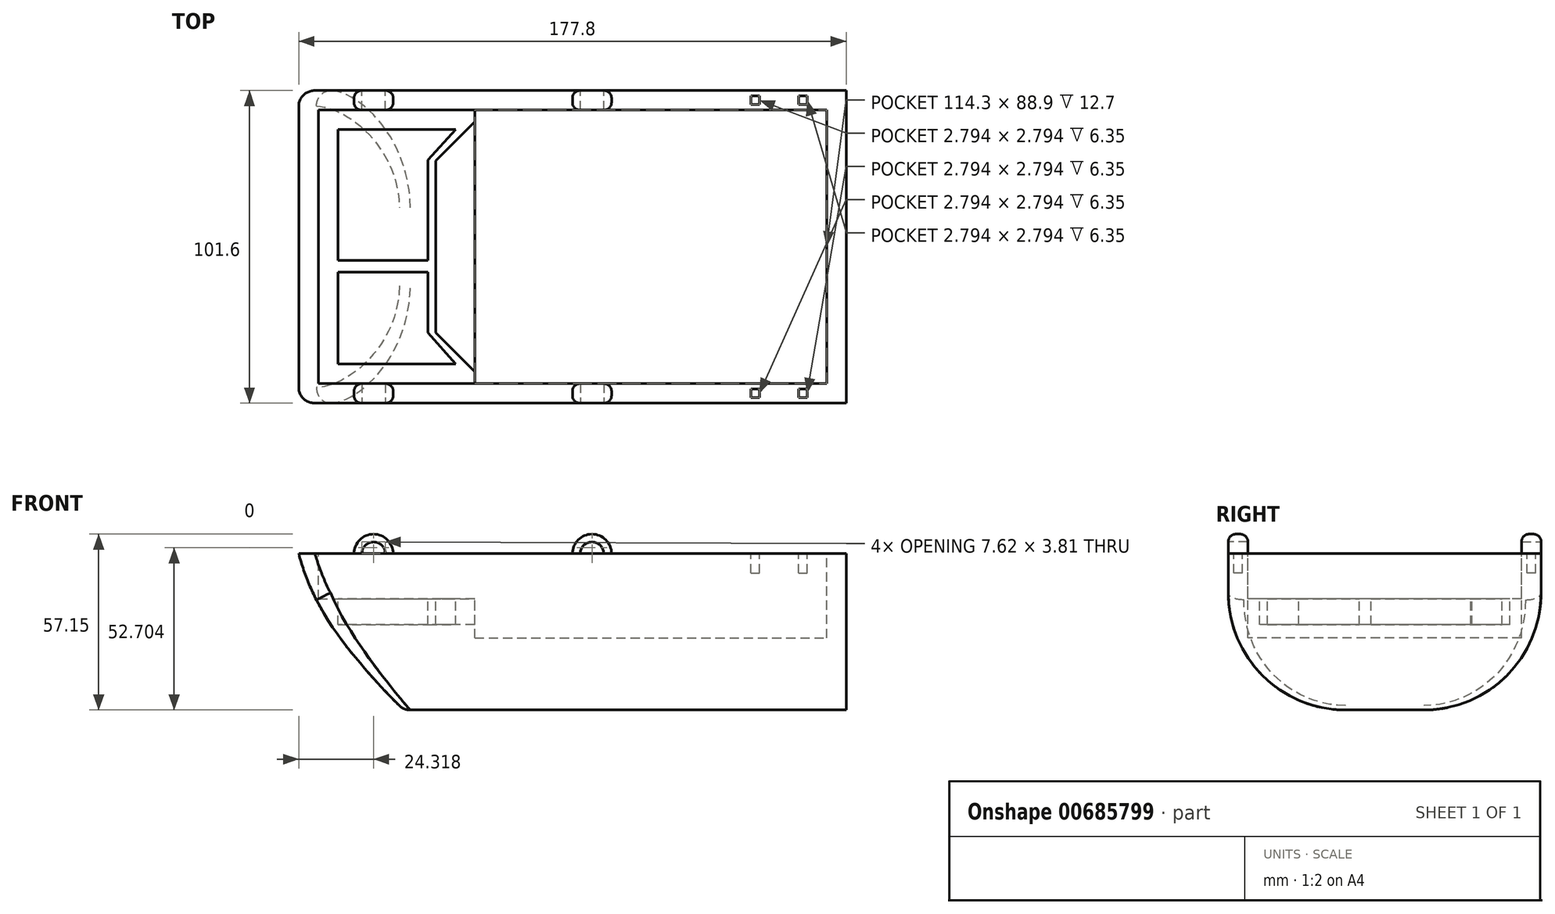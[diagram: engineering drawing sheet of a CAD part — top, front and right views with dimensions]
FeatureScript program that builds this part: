
annotation { "Feature Type Name" : "Feature", "Feature Type Description" : "" }
export const myFeature = defineFeature(function(context is Context, id is Id, definition is map)
    precondition{}
    {
        {
            var Q0;
            Q0=qCreatedBy(makeId("Front.planeOp"),FACE);
            var sketch = newSketch(context, id + "F0", { "sketchPlane" : qUnion([Q0])});
            skLineSegment(sketch, "E0.bottom", {"start": v(-88.38, 8.83) * mm, "end": v(89.42, 8.83) * mm});
            skLineSegment(sketch, "E0.top", {"start": v(-88.38, -41.97) * mm, "end": v(89.42, -41.97) * mm});
            skLineSegment(sketch, "E0.left", {"start": v(-88.38, 8.83) * mm, "end": v(-88.38, -41.97) * mm});
            skLineSegment(sketch, "E0.right", {"start": v(89.42, 8.83) * mm, "end": v(89.42, -41.97) * mm});
            skFitSpline(sketch, "E1", {"points": [v(-88.38, 8.83) * mm, v(-72.72, -21.5) * mm, v(-53.83, -41.97) * mm], "startDerivative": vector(13.28, -49.8) * mm, "endDerivative": vector(-11.54, 16.16) * mm});
            skFitSpline(sketch, "E2", {"points": [v(-53.83, -41.97) * mm, v(0, -44.03) * mm, v(89.42, -41.97) * mm], "startDerivative": vector(12.54, -17.55) * mm, "endDerivative": vector(155.33, 14.15) * mm});
            skSolve(sketch);
        }
        {
            var Q0;
            {var subQ0=sQuery(id+"F0.wireOp",EDGE,"E0.bottom");Q0=makeQuery(id+"F0.imprint","IMPRINT",FACE,{"disambiguationData":[TD([[makeQuery(id+"F0.imprint","IMPRINT",EDGE,{"derivedFrom":subQ0}),-1.0]])]});}
            extrude(context, id + "F1", {"entities" : qUnion([Q0]), "depth" : 101.6 * mm, "offsetDistance" : 25.4 * mm});
        }
        {
            var Q0;
            Q0=makeQuery(id+"F1.opExtrude","SWEPT_FACE",FACE,{"disambiguationData":[OSD([sQuery(id+"F0.wireOp",EDGE,"E0.bottom")])]});
            var sketch = newSketch(context, id + "F2", { "sketchPlane" : qUnion([Q0])});
            skLineSegment(sketch, "E3.bottom", {"start": v(-82.03, -6.35) * mm, "end": v(83.07, -6.35) * mm});
            skLineSegment(sketch, "E3.top", {"start": v(-82.03, -95.25) * mm, "end": v(83.07, -95.25) * mm});
            skLineSegment(sketch, "E3.left", {"start": v(-82.03, -6.35) * mm, "end": v(-82.03, -95.25) * mm});
            skLineSegment(sketch, "E3.right", {"start": v(83.07, -6.35) * mm, "end": v(83.07, -95.25) * mm});
            skSolve(sketch);
        }
        {
            var Q0;
            Q0=makeQuery(id+"F2.imprint","IMPRINT",FACE,{"disambiguationData":[TD([[makeQuery(id+"F2.imprint","IMPRINT",EDGE,{"derivedFrom":sQuery(id+"F2.wireOp",EDGE,"E3.bottom")}),-1.0]])]});
            extrude(context, id + "F3", {"entities" : qUnion([Q0]), "operationType" : NewBodyOperationType.REMOVE, "oppositeDirection" : true, "depth" : 14.73 * mm, "offsetDistance" : 25.4 * mm});
        }
        {
            var Q0;
            Q0=makeQuery(id+"F3.boolean.opBoolean","COPY",FACE,{"derivedFrom":makeQuery(id+"F3.opExtrude","CAP_FACE",FACE,{"disambiguationData":[OSD([sQuery(id+"F2.wireOp",EDGE,"E3.bottom"),sQuery(id+"F2.wireOp",EDGE,"E3.top"),sQuery(id+"F2.wireOp",EDGE,"E3.left"),sQuery(id+"F2.wireOp",EDGE,"E3.right")])],"isStart":false})});
            var sketch = newSketch(context, id + "F4", { "sketchPlane" : qUnion([Q0])});
            skLineSegment(sketch, "E4.bottom", {"start": v(-31.23, -6.35) * mm, "end": v(83.07, -6.35) * mm});
            skLineSegment(sketch, "E4.top", {"start": v(-31.23, -95.25) * mm, "end": v(83.07, -95.25) * mm});
            skLineSegment(sketch, "E4.left", {"start": v(-31.23, -6.35) * mm, "end": v(-31.23, -95.25) * mm});
            skLineSegment(sketch, "E4.right", {"start": v(83.07, -6.35) * mm, "end": v(83.07, -95.25) * mm});
            skSolve(sketch);
        }
        {
            var Q0;
            Q0 = qSketchRegion(id + "F4", true);
            extrude(context, id + "F5", {"entities" : qUnion([Q0]), "operationType" : NewBodyOperationType.REMOVE, "oppositeDirection" : true, "depth" : 12.7 * mm, "offsetDistance" : 25.4 * mm});
        }
        {
            var Q0;
            Q0=makeQuery(id+"F1.opExtrude","CAP_EDGE",EDGE,{"disambiguationData":[OSD([sQuery(id+"F0.wireOp",EDGE,"E0.top")])],"isStart":false});
            fillet(context, id + "F6", {"entities" : qUnion([Q0]), "radius" : 38.1 * mm, "tangentPropagation" : true, "allowEdgeOverflow" : false});
        }
        {
            var Q0;
            Q0=makeQuery(id+"F1.opExtrude","CAP_EDGE",EDGE,{"disambiguationData":[OSD([sQuery(id+"F0.wireOp",EDGE,"E0.top")])],"isStart":true});
            fillet(context, id + "F7", {"entities" : qUnion([Q0]), "radius" : 38.1 * mm, "tangentPropagation" : true, "allowEdgeOverflow" : false});
        }
        {
            var Q0;
            Q0=makeQuery(id+"F1.opExtrude","SWEPT_EDGE",EDGE,{"disambiguationData":[OSD([sQuery(id+"F0.wireOp",EDGE,"E0.top"),sQuery(id+"F0.wireOp",EDGE,"E1")])]});
            fillet(context, id + "F8", {"entities" : qUnion([Q0]), "radius" : 5.08 * mm, "tangentPropagation" : true, "allowEdgeOverflow" : false});
        }
        {
            var Q0;
            Q0=makeQuery(id+"F3.boolean.opBoolean","COPY",FACE,{"derivedFrom":makeQuery(id+"F3.opExtrude","CAP_FACE",FACE,{"disambiguationData":[OSD([sQuery(id+"F2.wireOp",EDGE,"E3.bottom"),sQuery(id+"F2.wireOp",EDGE,"E3.top"),sQuery(id+"F2.wireOp",EDGE,"E3.left"),sQuery(id+"F2.wireOp",EDGE,"E3.right")])],"isStart":false})});
            var sketch = newSketch(context, id + "F9", { "sketchPlane" : qUnion([Q0])});
            skLineSegment(sketch, "E5.bottom", {"start": v(-78.22, -10.16) * mm, "end": v(-31.23, -10.16) * mm});
            skLineSegment(sketch, "E5.top", {"start": v(-78.22, -91.44) * mm, "end": v(-31.23, -91.44) * mm});
            skLineSegment(sketch, "E5.left", {"start": v(-78.22, -10.16) * mm, "end": v(-78.22, -91.44) * mm});
            skLineSegment(sketch, "E5.right", {"start": v(-31.23, -10.16) * mm, "end": v(-31.23, -91.44) * mm});
            skLineSegment(sketch, "E6", {"start": v(-31.23, -10.16) * mm, "end": v(-43.93, -22.86) * mm});
            skLineSegment(sketch, "E7", {"start": v(-43.93, -78.74) * mm, "end": v(-31.23, -91.44) * mm});
            skLineSegment(sketch, "E8", {"start": v(-43.93, -22.86) * mm, "end": v(-43.93, -78.74) * mm});
            skLineSegment(sketch, "E9", {"start": v(-75.68, -12.7) * mm, "end": v(-75.68, -88.9) * mm});
            skLineSegment(sketch, "E10", {"start": v(-75.68, -88.9) * mm, "end": v(-37.36, -88.9) * mm});
            skLineSegment(sketch, "E11", {"start": v(-37.36, -88.9) * mm, "end": v(-46.47, -78.74) * mm});
            skLineSegment(sketch, "E12", {"start": v(-46.47, -78.74) * mm, "end": v(-46.47, -22.51) * mm});
            skLineSegment(sketch, "E13", {"start": v(-46.47, -22.51) * mm, "end": v(-37.36, -12.7) * mm});
            skLineSegment(sketch, "E14", {"start": v(-37.36, -12.7) * mm, "end": v(-75.68, -12.7) * mm});
            skLineSegment(sketch, "E15", {"start": v(-75.68, -59.06) * mm, "end": v(-46.47, -59.06) * mm});
            skLineSegment(sketch, "E16", {"start": v(-75.68, -55.25) * mm, "end": v(-46.47, -55.25) * mm});
            skSolve(sketch);
        }
        {
            var Q0;
            Q0=makeQuery(id+"F9.imprint","IMPRINT",FACE,{"disambiguationData":[TD([[makeQuery(id+"F9.imprint","IMPRINT",EDGE,{"derivedFrom":sQuery(id+"F9.wireOp",EDGE,"E5.right")}),-1.0]])]});
            var Q1;
            {var subQ1=sQuery(id+"F9.wireOp",EDGE,"E13");Q1=makeQuery(id+"F9.imprint","IMPRINT",FACE,{"disambiguationData":[TD([[makeQuery(id+"F9.imprint","IMPRINT",EDGE,{"derivedFrom":subQ1}),1.0]])]});}
            var Q2;
            {var subQ3=sQuery(id+"F9.wireOp",EDGE,"E10");Q2=makeQuery(id+"F9.imprint","IMPRINT",FACE,{"disambiguationData":[TD([[makeQuery(id+"F9.imprint","IMPRINT",EDGE,{"derivedFrom":subQ3}),1.0]])]});}
            extrude(context, id + "F10", {"entities" : qUnion([Q0, Q1, Q2]), "operationType" : NewBodyOperationType.REMOVE, "oppositeDirection" : true, "depth" : 8.38 * mm, "offsetDistance" : 25.4 * mm});
        }
        {
            var Q0;
            Q0=makeQuery(id+"F1.opExtrude","CAP_FACE",FACE,{"disambiguationData":[OSD([sQuery(id+"F0.wireOp",EDGE,"E0.bottom"),sQuery(id+"F0.wireOp",EDGE,"E0.top"),sQuery(id+"F0.wireOp",EDGE,"E0.right"),sQuery(id+"F0.wireOp",EDGE,"E1")])],"isStart":false});
            var sketch = newSketch(context, id + "F11", { "sketchPlane" : qUnion([Q0])});
            skCircle(sketch, "E17", {"center": v(-64.06, 8.83) * mm, "radius": 6.35 * mm});
            skCircle(sketch, "E18", {"center": v(6.87, 8.83) * mm, "radius": 6.35 * mm});
            skCircle(sketch, "E19", {"center": v(-64.06, 8.83) * mm, "radius": 3.81 * mm});
            skCircle(sketch, "E20", {"center": v(6.87, 8.83) * mm, "radius": 3.81 * mm});
            skSolve(sketch);
        }
        {
            var Q0;
            {var subQ0=sQuery(id+"F11.wireOp",EDGE,"E17");var subQ1=makeQuery(id+"F1.opExtrude","CAP_EDGE",EDGE,{"disambiguationData":[OSD([sQuery(id+"F0.wireOp",EDGE,"E0.bottom")])],"isStart":false});var subQ2=makeQuery(id+"F11.imprint","INTERSECT",VERTEX,{"disambiguationData":[OD(0.0)],"derivedFrom":[subQ1,subQ0]});Q0=makeQuery(id+"F11.imprint","IMPRINT",FACE,{"disambiguationData":[TD([[makeQuery(id+"F11.imprint","IMPRINT",EDGE,{"disambiguationData":[TD([[subQ2,1.0]])],"derivedFrom":subQ0}),1.0]])]});}
            var Q1;
            {var subQ0=sQuery(id+"F11.wireOp",EDGE,"E18");var subQ1=makeQuery(id+"F1.opExtrude","CAP_EDGE",EDGE,{"disambiguationData":[OSD([sQuery(id+"F0.wireOp",EDGE,"E0.bottom")])],"isStart":false});var subQ2=makeQuery(id+"F11.imprint","INTERSECT",VERTEX,{"disambiguationData":[OD(0.0)],"derivedFrom":[subQ1,subQ0]});Q1=makeQuery(id+"F11.imprint","IMPRINT",FACE,{"disambiguationData":[TD([[makeQuery(id+"F11.imprint","IMPRINT",EDGE,{"disambiguationData":[TD([[subQ2,-1.0]])],"derivedFrom":subQ0}),1.0]])]});}
            extrude(context, id + "F12", {"entities" : qUnion([Q0, Q1]), "operationType" : NewBodyOperationType.ADD, "oppositeDirection" : true, "depth" : 6.35 * mm, "offsetDistance" : 25.4 * mm});
        }
        {
            var Q0;
            Q0=makeQuery(id+"F12.opExtrude","CAP_EDGE",EDGE,{"disambiguationData":[OSD([sQuery(id+"F11.wireOp",EDGE,"E17")])],"isStart":true});
            var Q1;
            Q1=makeQuery(id+"F12.opExtrude","CAP_EDGE",EDGE,{"disambiguationData":[OSD([sQuery(id+"F11.wireOp",EDGE,"E17")])],"isStart":false});
            var Q2;
            Q2=makeQuery(id+"F12.opExtrude","CAP_EDGE",EDGE,{"disambiguationData":[OSD([sQuery(id+"F11.wireOp",EDGE,"E18")])],"isStart":false});
            var Q3;
            Q3=makeQuery(id+"F12.opExtrude","CAP_EDGE",EDGE,{"disambiguationData":[OSD([sQuery(id+"F11.wireOp",EDGE,"E18")])],"isStart":true});
            fillet(context, id + "F13", {"entities" : qUnion([Q0, Q1, Q2, Q3]), "radius" : 2.41 * mm, "tangentPropagation" : true, "allowEdgeOverflow" : false});
        }
        {
            var Q0;
            Q0=makeQuery(id+"F1.opExtrude","CAP_FACE",FACE,{"disambiguationData":[OSD([sQuery(id+"F0.wireOp",EDGE,"E0.bottom"),sQuery(id+"F0.wireOp",EDGE,"E0.top"),sQuery(id+"F0.wireOp",EDGE,"E0.right"),sQuery(id+"F0.wireOp",EDGE,"E1")])],"isStart":true});
            var sketch = newSketch(context, id + "F14", { "sketchPlane" : qUnion([Q0])});
            skCircle(sketch, "E21", {"center": v(-6.87, 8.83) * mm, "radius": 6.35 * mm});
            skCircle(sketch, "E22", {"center": v(64.06, 8.83) * mm, "radius": 6.35 * mm});
            skCircle(sketch, "E23", {"center": v(-6.87, 8.83) * mm, "radius": 3.81 * mm});
            skCircle(sketch, "E24", {"center": v(64.06, 8.83) * mm, "radius": 3.81 * mm});
            skSolve(sketch);
        }
        {
            var Q0;
            {var subQ0=sQuery(id+"F14.wireOp",EDGE,"E21");var subQ1=makeQuery(id+"F1.opExtrude","CAP_EDGE",EDGE,{"disambiguationData":[OSD([sQuery(id+"F0.wireOp",EDGE,"E0.bottom")])],"isStart":true});var subQ2=makeQuery(id+"F14.imprint","INTERSECT",VERTEX,{"disambiguationData":[OD(0.0)],"derivedFrom":[subQ1,subQ0]});Q0=makeQuery(id+"F14.imprint","IMPRINT",FACE,{"disambiguationData":[TD([[makeQuery(id+"F14.imprint","IMPRINT",EDGE,{"disambiguationData":[TD([[subQ2,1.0]])],"derivedFrom":subQ0}),1.0]])]});}
            var Q1;
            {var subQ0=sQuery(id+"F14.wireOp",EDGE,"E22");var subQ1=makeQuery(id+"F1.opExtrude","CAP_EDGE",EDGE,{"disambiguationData":[OSD([sQuery(id+"F0.wireOp",EDGE,"E0.bottom")])],"isStart":true});var subQ2=makeQuery(id+"F14.imprint","INTERSECT",VERTEX,{"disambiguationData":[OD(0.0)],"derivedFrom":[subQ1,subQ0]});Q1=makeQuery(id+"F14.imprint","IMPRINT",FACE,{"disambiguationData":[TD([[makeQuery(id+"F14.imprint","IMPRINT",EDGE,{"disambiguationData":[TD([[subQ2,-1.0]])],"derivedFrom":subQ0}),1.0]])]});}
            extrude(context, id + "F15", {"entities" : qUnion([Q0, Q1]), "operationType" : NewBodyOperationType.ADD, "oppositeDirection" : true, "depth" : 6.35 * mm, "offsetDistance" : 25.4 * mm});
        }
        {
            var Q0;
            Q0=makeQuery(id+"F15.opExtrude","CAP_EDGE",EDGE,{"disambiguationData":[OSD([sQuery(id+"F14.wireOp",EDGE,"E21")])],"isStart":true});
            var Q1;
            Q1=makeQuery(id+"F15.opExtrude","CAP_EDGE",EDGE,{"disambiguationData":[OSD([sQuery(id+"F14.wireOp",EDGE,"E21")])],"isStart":false});
            var Q2;
            Q2=makeQuery(id+"F15.opExtrude","CAP_EDGE",EDGE,{"disambiguationData":[OSD([sQuery(id+"F14.wireOp",EDGE,"E22")])],"isStart":true});
            var Q3;
            Q3=makeQuery(id+"F15.opExtrude","CAP_EDGE",EDGE,{"disambiguationData":[OSD([sQuery(id+"F14.wireOp",EDGE,"E22")])],"isStart":false});
            fillet(context, id + "F16", {"entities" : qUnion([Q0, Q1, Q2, Q3]), "radius" : 2.41 * mm, "tangentPropagation" : true, "allowEdgeOverflow" : false});
        }
        {
            var Q0;
            {var subQ0=makeQuery(id+"F5.opExtrude","SWEPT_FACE",FACE,{"disambiguationData":[OSD([sQuery(id+"F4.wireOp",EDGE,"E4.right")])]});var subQ1=sQuery(id+"F11.wireOp",EDGE,"E18");var subQ2=makeQuery(id+"F5.opExtrude","SWEPT_FACE",FACE,{"disambiguationData":[OSD([sQuery(id+"F4.wireOp",EDGE,"E4.bottom")])]});var subQ3=makeQuery(id+"F3.boolean.opBoolean","COPY",FACE,{"derivedFrom":makeQuery(id+"F3.opExtrude","SWEPT_FACE",FACE,{"disambiguationData":[OSD([sQuery(id+"F2.wireOp",EDGE,"E3.right")])]})});var subQ4=makeQuery(id+"F5.opExtrude","SWEPT_FACE",FACE,{"disambiguationData":[OSD([sQuery(id+"F4.wireOp",EDGE,"E4.top")])]});var subQ5=sQuery(id+"F11.wireOp",EDGE,"E19");var subQ6=sQuery(id+"F11.wireOp",EDGE,"E17");var subQ7=sQuery(id+"F0.wireOp",EDGE,"E0.bottom");var subQ8=makeQuery(id+"F12.opExtrude","CAP_FACE",FACE,{"disambiguationData":[OSD([subQ7,subQ6,subQ5])],"isStart":true});var subQ9=sQuery(id+"F0.wireOp",EDGE,"E1");var subQ10=sQuery(id+"F0.wireOp",EDGE,"E0.right");var subQ11=sQuery(id+"F0.wireOp",EDGE,"E0.top");var subQ12=makeQuery(id+"F1.opExtrude","CAP_FACE",FACE,{"disambiguationData":[OSD([subQ7,subQ11,subQ10,subQ9])],"isStart":false});var subQ13=sQuery(id+"F14.wireOp",EDGE,"E23");var subQ14=sQuery(id+"F14.wireOp",EDGE,"E21");var subQ15=makeQuery(id+"F3.boolean.opBoolean","COPY",FACE,{"derivedFrom":makeQuery(id+"F3.opExtrude","SWEPT_FACE",FACE,{"disambiguationData":[OSD([sQuery(id+"F2.wireOp",EDGE,"E3.top")])]})});var subQ16=makeQuery(id+"F1.opExtrude","CAP_FACE",FACE,{"disambiguationData":[OSD([subQ7,subQ11,subQ10,subQ9])],"isStart":true});var subQ17=makeQuery(id+"F1.opExtrude","SWEPT_FACE",FACE,{"disambiguationData":[OSD([subQ10])]});var subQ18=makeQuery(id+"F12.opExtrude","SWEPT_FACE",FACE,{"disambiguationData":[OSD([subQ1])]});var subQ19=sQuery(id+"F14.wireOp",EDGE,"E24");var subQ20=sQuery(id+"F14.wireOp",EDGE,"E22");var subQ21=makeQuery(id+"F3.boolean.opBoolean","COPY",FACE,{"derivedFrom":makeQuery(id+"F3.opExtrude","SWEPT_FACE",FACE,{"disambiguationData":[OSD([sQuery(id+"F2.wireOp",EDGE,"E3.bottom")])]})});var subQ22=makeQuery(id+"F12.opExtrude","CAP_FACE",FACE,{"disambiguationData":[OSD([subQ7,subQ6,subQ5])],"isStart":false});var subQ23=sQuery(id+"F11.wireOp",EDGE,"E20");var subQ24=makeQuery(id+"F12.opExtrude","CAP_FACE",FACE,{"disambiguationData":[OSD([subQ7,subQ1,subQ23])],"isStart":true});var subQ25=makeQuery(id+"F12.opExtrude","CAP_FACE",FACE,{"disambiguationData":[OSD([subQ7,subQ1,subQ23])],"isStart":false});Q0=makeQuery(id+"F15.boolean.opBoolean","SPLIT",FACE,{"disambiguationData":[TD([subQ16,subQ12,subQ17,subQ21,subQ15,subQ3,subQ2,subQ4,subQ0,subQ8,subQ22,subQ18,subQ24,subQ25,makeQuery(id+"F13.opFillet","BLEND_FACE",FACE,{"disambiguationData":[OSD([subQ1]),TDD([makeQuery(id+"F12.opExtrude","CAP_EDGE",EDGE,{"disambiguationData":[OSD([subQ1])],"isStart":true})])]}),makeQuery(id+"F13.opFillet","BLEND_FACE",FACE,{"disambiguationData":[OSD([subQ1]),TDD([makeQuery(id+"F12.opExtrude","CAP_EDGE",EDGE,{"disambiguationData":[OSD([subQ1])],"isStart":false})])]}),makeQuery(id+"F15.opExtrude","SWEPT_FACE",FACE,{"disambiguationData":[OSD([subQ14])]}),makeQuery(id+"F15.opExtrude","CAP_FACE",FACE,{"disambiguationData":[OSD([subQ7,subQ14,subQ13])],"isStart":true}),makeQuery(id+"F15.opExtrude","CAP_FACE",FACE,{"disambiguationData":[OSD([subQ7,subQ14,subQ13])],"isStart":false}),makeQuery(id+"F15.opExtrude","CAP_FACE",FACE,{"disambiguationData":[OSD([subQ7,subQ20,subQ19])],"isStart":true}),makeQuery(id+"F15.opExtrude","CAP_FACE",FACE,{"disambiguationData":[OSD([subQ7,subQ20,subQ19])],"isStart":false})])],"derivedFrom":makeQuery(id+"F12.boolean.opBoolean","SPLIT",FACE,{"disambiguationData":[TD([subQ16,subQ12,subQ17,makeQuery(id+"F1.opExtrude","SWEPT_FACE",FACE,{"disambiguationData":[OSD([subQ9])]}),subQ21,subQ15,makeQuery(id+"F3.boolean.opBoolean","COPY",FACE,{"derivedFrom":makeQuery(id+"F3.opExtrude","SWEPT_FACE",FACE,{"disambiguationData":[OSD([sQuery(id+"F2.wireOp",EDGE,"E3.left")])]})}),subQ3,subQ2,subQ4,subQ0,makeQuery(id+"F8.opFillet","BLEND_FACE",FACE,{"disambiguationData":[OSD([subQ9]),TDD([makeQuery(id+"F1.opExtrude","CAP_EDGE",EDGE,{"disambiguationData":[OSD([subQ9])],"isStart":true})])]}),makeQuery(id+"F8.opFillet","BLEND_FACE",FACE,{"disambiguationData":[OSD([subQ9]),TDD([makeQuery(id+"F1.opExtrude","CAP_EDGE",EDGE,{"disambiguationData":[OSD([subQ9])],"isStart":false})]),OD(0.0)]}),makeQuery(id+"F12.opExtrude","SWEPT_FACE",FACE,{"disambiguationData":[OSD([subQ6])]}),subQ8,subQ22,subQ18,subQ24,subQ25])],"derivedFrom":makeQuery(id+"F1.opExtrude","SWEPT_FACE",FACE,{"disambiguationData":[OSD([subQ7])]})})});}
            var sketch = newSketch(context, id + "F17", { "sketchPlane" : qUnion([Q0])});
            skLineSegment(sketch, "E25.bottom", {"start": v(58.43, -1.78) * mm, "end": v(61.22, -1.78) * mm});
            skLineSegment(sketch, "E25.top", {"start": v(58.43, -4.57) * mm, "end": v(61.22, -4.57) * mm});
            skLineSegment(sketch, "E25.left", {"start": v(58.43, -1.78) * mm, "end": v(58.43, -4.57) * mm});
            skLineSegment(sketch, "E25.right", {"start": v(61.22, -1.78) * mm, "end": v(61.22, -4.57) * mm});
            skLineSegment(sketch, "E26.bottom", {"start": v(73.92, -1.78) * mm, "end": v(76.72, -1.78) * mm});
            skLineSegment(sketch, "E26.top", {"start": v(73.92, -4.57) * mm, "end": v(76.72, -4.57) * mm});
            skLineSegment(sketch, "E26.left", {"start": v(73.92, -1.78) * mm, "end": v(73.92, -4.57) * mm});
            skLineSegment(sketch, "E26.right", {"start": v(76.72, -1.78) * mm, "end": v(76.72, -4.57) * mm});
            skLineSegment(sketch, "E27.bottom", {"start": v(58.43, -97.03) * mm, "end": v(61.22, -97.03) * mm});
            skLineSegment(sketch, "E27.top", {"start": v(58.43, -99.82) * mm, "end": v(61.22, -99.82) * mm});
            skLineSegment(sketch, "E27.left", {"start": v(58.43, -97.03) * mm, "end": v(58.43, -99.82) * mm});
            skLineSegment(sketch, "E27.right", {"start": v(61.22, -97.03) * mm, "end": v(61.22, -99.82) * mm});
            skLineSegment(sketch, "E28.bottom", {"start": v(73.92, -97.03) * mm, "end": v(76.72, -97.03) * mm});
            skLineSegment(sketch, "E28.top", {"start": v(73.92, -99.82) * mm, "end": v(76.72, -99.82) * mm});
            skLineSegment(sketch, "E28.left", {"start": v(73.92, -97.03) * mm, "end": v(73.92, -99.82) * mm});
            skLineSegment(sketch, "E28.right", {"start": v(76.72, -97.03) * mm, "end": v(76.72, -99.82) * mm});
            skSolve(sketch);
        }
        {
            var Q0;
            Q0=makeQuery(id+"F17.imprint","IMPRINT",FACE,{"disambiguationData":[TD([[makeQuery(id+"F17.imprint","IMPRINT",EDGE,{"derivedFrom":sQuery(id+"F17.wireOp",EDGE,"E25.bottom")}),-1.0]])]});
            var Q1;
            Q1=makeQuery(id+"F17.imprint","IMPRINT",FACE,{"disambiguationData":[TD([[makeQuery(id+"F17.imprint","IMPRINT",EDGE,{"derivedFrom":sQuery(id+"F17.wireOp",EDGE,"E26.bottom")}),-1.0]])]});
            var Q2;
            Q2=makeQuery(id+"F17.imprint","IMPRINT",FACE,{"disambiguationData":[TD([[makeQuery(id+"F17.imprint","IMPRINT",EDGE,{"derivedFrom":sQuery(id+"F17.wireOp",EDGE,"E27.bottom")}),-1.0]])]});
            var Q3;
            Q3=makeQuery(id+"F17.imprint","IMPRINT",FACE,{"disambiguationData":[TD([[makeQuery(id+"F17.imprint","IMPRINT",EDGE,{"derivedFrom":sQuery(id+"F17.wireOp",EDGE,"E28.bottom")}),-1.0]])]});
            extrude(context, id + "F18", {"entities" : qUnion([Q0, Q1, Q2, Q3]), "operationType" : NewBodyOperationType.REMOVE, "oppositeDirection" : true, "depth" : 6.35 * mm, "offsetDistance" : 25.4 * mm});
        }
    });
